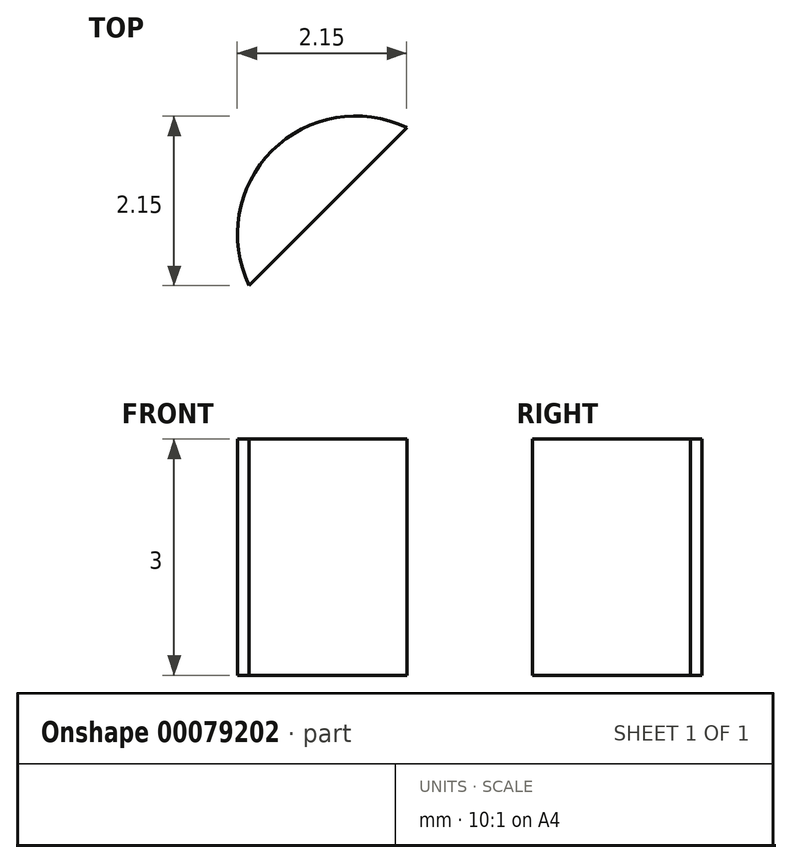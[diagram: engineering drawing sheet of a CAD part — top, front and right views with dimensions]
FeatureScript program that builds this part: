
annotation { "Feature Type Name" : "Feature", "Feature Type Description" : "" }
export const myFeature = defineFeature(function(context is Context, id is Id, definition is map)
    precondition{}
    {
        {
            var Q0;
            Q0=qCreatedBy(makeId("Top.planeOp"),FACE);
            var sketch = newSketch(context, id + "F0", { "sketchPlane" : qUnion([Q0])});
            skFitSpline(sketch, "E0.0.0", {"points": [v(-191, 0) * mm, v(-191, -31) * mm, v(-159.74, -92.2) * mm, v(-184.76, -197.17) * mm, v(-196.84, -201.33) * mm, v(-195.38, -204.68) * mm, v(-191.45, -211.03) * mm, v(-181.99, -213.22) * mm, v(-179.14, -216) * mm, v(-179.15, -231.75) * mm, v(-173.66, -257.8) * mm, v(-156.24, -267.72) * mm, v(-139.3, -271.16) * mm, v(-124.5, -267.12) * mm, v(-95.07, -253.88) * mm, v(-89.85, -257.77) * mm, v(-87.34, -261.97) * mm, v(-79.14, -275.56) * mm, v(0, -317.47) * mm, v(79.14, -275.56) * mm, v(87.34, -261.97) * mm, v(89.85, -257.77) * mm, v(95.07, -253.88) * mm, v(124.5, -267.11) * mm, v(139.3, -271.16) * mm, v(156.3, -267.7) * mm, v(173.4, -257.87) * mm, v(180.16, -231.44) * mm, v(176.53, -214.3) * mm, v(191.5, -211.34) * mm, v(195.34, -204.69) * mm, v(196.86, -201.33) * mm, v(184.74, -197.18) * mm, v(159.75, -92.2) * mm, v(206.83, 0) * mm, v(159.75, 92.2) * mm, v(184.74, 197.18) * mm, v(196.86, 201.33) * mm, v(195.34, 204.69) * mm, v(191.5, 211.34) * mm, v(176.53, 214.3) * mm, v(180.16, 231.44) * mm, v(173.4, 257.87) * mm, v(156.3, 267.7) * mm, v(139.3, 271.16) * mm, v(124.5, 267.11) * mm, v(95.07, 253.88) * mm, v(89.85, 257.77) * mm, v(87.34, 261.97) * mm, v(79.14, 275.56) * mm, v(0, 317.47) * mm, v(-79.14, 275.56) * mm, v(-87.34, 261.97) * mm, v(-89.85, 257.77) * mm, v(-95.07, 253.88) * mm, v(-124.5, 267.12) * mm, v(-139.3, 271.16) * mm, v(-156.24, 267.72) * mm, v(-173.66, 257.8) * mm, v(-179.15, 231.75) * mm, v(-179.14, 216) * mm, v(-181.99, 213.22) * mm, v(-191.45, 211.03) * mm, v(-195.38, 204.68) * mm, v(-196.84, 201.33) * mm, v(-184.76, 197.17) * mm, v(-159.74, 92.2) * mm, v(-191, 31) * mm, v(-191, 0) * mm]});
            skCircle(sketch, "E1.0", {"center": v(0, 192.5) * mm, "radius": 6 * mm});
            skCircle(sketch, "E2.0", {"center": v(0, -192.5) * mm, "radius": 6 * mm});
            skPoint(sketch, "E3.0", {"position": v(0, 0) * mm});
            skLineSegment(sketch, "E4", {"start": v(-243.03, 0) * mm, "end": v(337.73, 0) * mm, "construction": true});
            skLineSegment(sketch, "E5", {"start": v(0, 337.07) * mm, "end": v(0, -343.4) * mm, "construction": true});
            skFitSpline(sketch, "E6.0.0", {"points": [v(-146.48, 0) * mm, v(-146.48, -31.99) * mm, v(-89.5, -87.65) * mm, v(-140.83, -150.23) * mm, v(0, -234.29) * mm, v(140.83, -150.23) * mm, v(89.5, -87.65) * mm, v(179.22, 0) * mm, v(89.5, 87.65) * mm, v(140.83, 150.23) * mm, v(0, 234.29) * mm, v(-140.83, 150.23) * mm, v(-89.5, 87.65) * mm, v(-146.48, 31.99) * mm, v(-146.48, 0) * mm]});
            skEllipticalArc(sketch, "E6.0.1", {});
            skFitSpline(sketch, "E6.0.2", {"points": [v(-146.48, 0) * mm, v(-146.48, -31.99) * mm, v(-89.5, -87.65) * mm, v(-140.83, -150.23) * mm, v(0, -234.29) * mm, v(140.83, -150.23) * mm, v(89.5, -87.65) * mm, v(179.22, 0) * mm, v(89.5, 87.65) * mm, v(140.83, 150.23) * mm, v(0, 234.29) * mm, v(-140.83, 150.23) * mm, v(-89.5, 87.65) * mm, v(-146.48, 31.99) * mm, v(-146.48, 0) * mm]});
            skEllipticalArc(sketch, "E6.0.3", {});
            skCircle(sketch, "E7.0", {"center": v(102.5, -75) * mm, "radius": 5 * mm});
            skCircle(sketch, "E8.0", {"center": v(102.5, 75) * mm, "radius": 5 * mm});
            skCircle(sketch, "E9.0", {"center": v(-102.5, 75) * mm, "radius": 5 * mm});
            skCircle(sketch, "E10.0", {"center": v(-102.5, -75) * mm, "radius": 5 * mm});
            skLineSegment(sketch, "E11", {"start": v(0, 300) * mm, "end": v(0, 202.46) * mm, "construction": true});
            skPoint(sketch, "E12", {"position": v(-191, 0) * mm});
            skPoint(sketch, "E13", {"position": v(0, -287.33) * mm});
            skPoint(sketch, "E14.MirrorP", {"position": v(-178.8, 0) * mm});
            skPoint(sketch, "E15.MirrorP", {"position": v(-161, -94.7) * mm});
            skPoint(sketch, "E16.MirrorP", {"position": v(-135.27, -192.3) * mm});
            skPoint(sketch, "E17", {"position": v(-173.78, -187.11) * mm});
            skPoint(sketch, "E18", {"position": v(-169.04, -211.96) * mm});
            skPoint(sketch, "E19", {"position": v(-172.92, -206.07) * mm});
            skPoint(sketch, "E20", {"position": v(-163.34, -243.8) * mm});
            skPoint(sketch, "E21", {"position": v(-112.98, -248.73) * mm});
            skPoint(sketch, "E22", {"position": v(-72.32, -260) * mm});
            skPoint(sketch, "E23", {"position": v(-82.35, -247.43) * mm});
            skPoint(sketch, "E24", {"position": v(-91.92, -242.99) * mm});
            skPoint(sketch, "E25", {"position": v(-144.07, -257.6) * mm});
            skPoint(sketch, "E26", {"position": v(-180.24, -201.62) * mm});
            skLineSegment(sketch, "E27", {"start": v(0, 0) * mm, "end": v(0, 248.44) * mm, "construction": true});
            skLineSegment(sketch, "E28", {"start": v(154, 0) * mm, "end": v(-100.29, 0) * mm, "construction": true});
            skPoint(sketch, "E29.MirrorP", {"position": v(0, 287.33) * mm});
            skPoint(sketch, "E30.MirrorP", {"position": v(-82.35, 247.43) * mm});
            skPoint(sketch, "E31.MirrorP", {"position": v(-172.92, 206.07) * mm});
            skPoint(sketch, "E32.MirrorP", {"position": v(-112.98, 248.73) * mm});
            skPoint(sketch, "E33.MirrorP", {"position": v(-163.34, 243.8) * mm});
            skPoint(sketch, "E34.MirrorP", {"position": v(-161, 94.7) * mm});
            skPoint(sketch, "E35.MirrorP", {"position": v(-169.04, 211.96) * mm});
            skPoint(sketch, "E36.MirrorP", {"position": v(-173.78, 187.11) * mm});
            skPoint(sketch, "E37.MirrorP", {"position": v(-144.07, 257.6) * mm});
            skPoint(sketch, "E38.MirrorP", {"position": v(-180.24, 201.62) * mm});
            skPoint(sketch, "E39.MirrorP", {"position": v(-72.32, 260) * mm});
            skPoint(sketch, "E40.MirrorP", {"position": v(-91.92, 242.99) * mm});
            skLineSegment(sketch, "E41.MirrorCS", {"start": v(0, 0) * mm, "end": v(0, -248.44) * mm, "construction": true});
            skPoint(sketch, "E42.MirrorP", {"position": v(180.24, -201.62) * mm});
            skPoint(sketch, "E43.MirrorP", {"position": v(178.8, 0) * mm});
            skPoint(sketch, "E44.MirrorP", {"position": v(180.25, 201.62) * mm});
            skPoint(sketch, "E45.MirrorP", {"position": v(0.01, 287.33) * mm});
            skPoint(sketch, "E46.MirrorP", {"position": v(91.91, -242.99) * mm});
            skPoint(sketch, "E47.MirrorP", {"position": v(72.33, 260) * mm});
            skPoint(sketch, "E48.MirrorP", {"position": v(163.34, 243.8) * mm});
            skPoint(sketch, "E49.MirrorP", {"position": v(82.34, -247.43) * mm});
            skPoint(sketch, "E50.MirrorP", {"position": v(173.77, -187.12) * mm});
            skPoint(sketch, "E51.MirrorP", {"position": v(161, -94.7) * mm});
            skPoint(sketch, "E52.MirrorP", {"position": v(72.32, -260) * mm});
            skPoint(sketch, "E53.MirrorP", {"position": v(82.35, 247.43) * mm});
            skPoint(sketch, "E54.MirrorP", {"position": v(173.78, 187.1) * mm});
            skPoint(sketch, "E55.MirrorP", {"position": v(169.03, -211.97) * mm});
            skPoint(sketch, "E56.MirrorP", {"position": v(169.04, 211.96) * mm});
            skPoint(sketch, "E57.MirrorP", {"position": v(163.33, -243.8) * mm});
            skPoint(sketch, "E58.MirrorP", {"position": v(161, 94.7) * mm});
            skPoint(sketch, "E59.MirrorP", {"position": v(172.92, 206.07) * mm});
            skPoint(sketch, "E60.MirrorP", {"position": v(144.07, 257.6) * mm});
            skPoint(sketch, "E61.MirrorP", {"position": v(112.97, -248.73) * mm});
            skPoint(sketch, "E62.MirrorP", {"position": v(112.98, 248.72) * mm});
            skPoint(sketch, "E63.MirrorP", {"position": v(91.92, 242.98) * mm});
            skPoint(sketch, "E64.MirrorP", {"position": v(144.06, -257.61) * mm});
            skPoint(sketch, "E65.MirrorP", {"position": v(172.91, -206.08) * mm});
            skFitSpline(sketch, "E66", {"points": [v(0, -287.33) * mm, v(-72.32, -260) * mm, v(-82.35, -247.43) * mm, v(-91.92, -242.99) * mm, v(-112.98, -248.73) * mm, v(-144.07, -257.6) * mm, v(-163.34, -243.8) * mm, v(-169.04, -211.96) * mm, v(-172.92, -206.07) * mm, v(-180.24, -201.62) * mm, v(-173.78, -187.11) * mm, v(-161, -94.7) * mm, v(-178.8, 0) * mm, v(-161, 94.7) * mm, v(-173.78, 187.11) * mm, v(-180.24, 201.62) * mm, v(-172.92, 206.07) * mm, v(-169.04, 211.96) * mm, v(-163.34, 243.8) * mm, v(-144.07, 257.6) * mm, v(-112.98, 248.73) * mm, v(-91.92, 242.99) * mm, v(-82.35, 247.43) * mm, v(-72.32, 260) * mm, v(0, 287.33) * mm, v(72.33, 260) * mm, v(82.35, 247.43) * mm, v(91.92, 242.98) * mm, v(112.98, 248.72) * mm, v(144.07, 257.6) * mm, v(163.34, 243.8) * mm, v(169.04, 211.96) * mm, v(172.92, 206.07) * mm, v(180.25, 201.62) * mm, v(173.78, 187.1) * mm, v(161, 94.7) * mm, v(178.8, 0) * mm, v(161, -94.7) * mm, v(173.77, -187.12) * mm, v(180.24, -201.62) * mm, v(172.91, -206.08) * mm, v(169.03, -211.97) * mm, v(163.33, -243.8) * mm, v(144.06, -257.61) * mm, v(112.97, -248.73) * mm, v(91.91, -242.99) * mm, v(82.34, -247.43) * mm, v(72.32, -260) * mm, v(0, -287.33) * mm]});
            skFitSpline(sketch, "E67.0", {"points": [v(142.65, 79.63) * mm, v(142.7, 82.88) * mm, v(142.65, 86.13) * mm, v(142.47, 90.44) * mm, v(142.03, 95.8) * mm, v(141.15, 102.18) * mm, v(139.52, 110.6) * mm, v(136.63, 120.92) * mm, v(131.87, 132.9) * mm, v(125.85, 144.38) * mm, v(119.83, 153.47) * mm, v(114.42, 160.4) * mm, v(110.08, 165.43) * mm, v(106.22, 169.46) * mm, v(103, 172.58) * mm, v(100.52, 174.88) * mm, v(97.98, 177.11) * mm, v(94.52, 180.01) * mm, v(90.06, 183.47) * mm, v(84.52, 187.36) * mm, v(76.88, 192.2) * mm, v(66.91, 197.57) * mm, v(54.35, 202.92) * mm, v(41.3, 207.13) * mm, v(30.08, 209.68) * mm, v(20.94, 211.11) * mm, v(14.01, 211.9) * mm, v(8.2, 212.28) * mm, v(3.52, 212.44) * mm, v(0, 212.48) * mm, v(-3.52, 212.44) * mm, v(-8.2, 212.28) * mm, v(-14.01, 211.9) * mm, v(-20.94, 211.11) * mm, v(-30.08, 209.68) * mm, v(-41.3, 207.13) * mm, v(-54.35, 202.92) * mm, v(-66.91, 197.57) * mm, v(-76.88, 192.2) * mm, v(-84.52, 187.36) * mm, v(-90.06, 183.47) * mm, v(-94.52, 180.01) * mm, v(-97.98, 177.11) * mm, v(-100.52, 174.88) * mm, v(-103, 172.58) * mm, v(-106.22, 169.46) * mm, v(-110.08, 165.43) * mm, v(-114.42, 160.4) * mm, v(-119.83, 153.47) * mm, v(-125.85, 144.38) * mm, v(-131.87, 132.9) * mm, v(-136.63, 120.92) * mm, v(-139.52, 110.6) * mm, v(-141.15, 102.18) * mm, v(-142.03, 95.8) * mm, v(-142.47, 90.44) * mm, v(-142.65, 86.13) * mm, v(-142.7, 82.88) * mm, v(-142.65, 79.63) * mm, v(-142.47, 75.32) * mm, v(-142.03, 69.96) * mm, v(-141.15, 63.58) * mm, v(-139.52, 55.16) * mm, v(-136.63, 44.84) * mm, v(-131.87, 32.86) * mm, v(-125.85, 21.38) * mm, v(-119.83, 12.3) * mm, v(-114.42, 5.36) * mm, v(-110.08, 0.34) * mm, v(-106.22, -3.7) * mm, v(-103, -6.82) * mm, v(-100.52, -9.12) * mm, v(-97.98, -11.35) * mm, v(-94.52, -14.25) * mm, v(-90.06, -17.7) * mm, v(-84.52, -21.6) * mm, v(-76.88, -26.44) * mm, v(-66.91, -31.8) * mm, v(-54.35, -37.16) * mm, v(-41.3, -41.37) * mm, v(-30.08, -43.92) * mm, v(-20.94, -45.35) * mm, v(-14.01, -46.13) * mm, v(-8.2, -46.52) * mm, v(-3.52, -46.68) * mm, v(0, -46.72) * mm, v(3.52, -46.68) * mm, v(8.2, -46.52) * mm, v(14.01, -46.13) * mm, v(20.94, -45.35) * mm, v(30.08, -43.92) * mm, v(41.3, -41.37) * mm, v(54.35, -37.16) * mm, v(66.91, -31.8) * mm, v(76.88, -26.44) * mm, v(84.52, -21.6) * mm, v(90.06, -17.7) * mm, v(94.52, -14.25) * mm, v(97.98, -11.35) * mm, v(100.52, -9.12) * mm, v(103, -6.82) * mm, v(106.22, -3.7) * mm, v(110.08, 0.34) * mm, v(114.42, 5.36) * mm, v(119.83, 12.3) * mm, v(125.85, 21.38) * mm, v(131.87, 32.86) * mm, v(136.63, 44.84) * mm, v(139.52, 55.16) * mm, v(141.15, 63.58) * mm, v(142.03, 69.96) * mm, v(142.47, 75.32) * mm, v(142.65, 79.63) * mm, v(142.7, 82.88) * mm, v(142.65, 86.13) * mm]});
            skFitSpline(sketch, "E67.1", {"points": [v(-156.44, 2.63) * mm, v(-156.5, 0) * mm, v(-156.44, -2.63) * mm, v(-156.27, -5.23) * mm, v(-155.98, -7.8) * mm, v(-155.47, -11.2) * mm, v(-154.6, -15.39) * mm, v(-153.23, -20.3) * mm, v(-151.6, -25.1) * mm, v(-149.11, -31.37) * mm, v(-145.56, -38.98) * mm, v(-140.87, -47.75) * mm, v(-136.06, -56.17) * mm, v(-131.4, -64.24) * mm, v(-127.89, -70.62) * mm, v(-125.43, -75.48) * mm, v(-123.8, -78.98) * mm, v(-122.4, -82.33) * mm, v(-121.28, -85.5) * mm, v(-120.58, -87.96) * mm, v(-120.16, -89.82) * mm, v(-119.97, -90.93) * mm, v(-119.85, -91.8) * mm, v(-119.74, -92.65) * mm, v(-119.66, -93.72) * mm, v(-119.6, -95.02) * mm, v(-119.61, -96.75) * mm, v(-119.75, -98.96) * mm, v(-120.1, -101.68) * mm, v(-120.63, -104.5) * mm, v(-121.51, -108.4) * mm, v(-122.88, -113.52) * mm, v(-124.62, -120.16) * mm, v(-125.79, -126.17) * mm, v(-126.28, -131.32) * mm, v(-126.34, -135.36) * mm, v(-126.02, -139.54) * mm, v(-125.42, -142.76) * mm, v(-124.86, -144.92) * mm, v(-124.44, -146.37) * mm, v(-123.84, -148.16) * mm, v(-123, -150.27) * mm, v(-121.73, -153.05) * mm, v(-119.89, -156.44) * mm, v(-117.3, -160.4) * mm, v(-114.36, -164.24) * mm, v(-110, -169.23) * mm, v(-103.8, -175.22) * mm, v(-95.22, -182) * mm, v(-85.64, -188.33) * mm, v(-75.18, -194.13) * mm, v(-63.93, -199.32) * mm, v(-52.02, -203.8) * mm, v(-39.56, -207.5) * mm, v(-28.81, -209.82) * mm, v(-20.05, -211.16) * mm, v(-13.42, -211.9) * mm, v(-7.84, -212.28) * mm, v(-3.37, -212.44) * mm, v(0, -212.48) * mm, v(3.37, -212.44) * mm, v(7.84, -212.28) * mm, v(13.42, -211.9) * mm, v(20.05, -211.16) * mm, v(28.81, -209.82) * mm, v(39.56, -207.5) * mm, v(52.02, -203.8) * mm, v(63.93, -199.32) * mm, v(75.18, -194.13) * mm, v(85.64, -188.33) * mm, v(95.22, -182) * mm, v(103.8, -175.22) * mm, v(110, -169.23) * mm, v(114.36, -164.24) * mm, v(117.3, -160.4) * mm, v(119.89, -156.44) * mm, v(121.73, -153.05) * mm, v(123, -150.27) * mm, v(123.84, -148.16) * mm, v(124.44, -146.37) * mm, v(124.86, -144.92) * mm, v(125.42, -142.76) * mm, v(126.02, -139.54) * mm, v(126.34, -135.36) * mm, v(126.28, -131.32) * mm, v(125.79, -126.17) * mm, v(124.62, -120.16) * mm, v(122.88, -113.52) * mm, v(121.51, -108.4) * mm, v(120.63, -104.5) * mm, v(120.1, -101.68) * mm, v(119.75, -98.96) * mm, v(119.61, -96.75) * mm, v(119.6, -95.02) * mm, v(119.66, -93.72) * mm, v(119.74, -92.65) * mm, v(119.85, -91.8) * mm, v(119.97, -90.93) * mm, v(120.16, -89.82) * mm, v(120.58, -87.96) * mm, v(121.28, -85.5) * mm, v(122.4, -82.33) * mm, v(123.8, -78.98) * mm, v(125.43, -75.48) * mm, v(127.89, -70.62) * mm, v(131.4, -64.24) * mm, v(136.06, -56.17) * mm, v(140.87, -47.75) * mm, v(145.56, -38.98) * mm, v(149.11, -31.37) * mm, v(151.6, -25.1) * mm, v(153.23, -20.3) * mm, v(154.6, -15.39) * mm, v(155.47, -11.2) * mm, v(155.98, -7.8) * mm, v(156.27, -5.23) * mm, v(156.44, -2.63) * mm, v(156.5, 0) * mm, v(156.44, 2.63) * mm, v(156.27, 5.23) * mm, v(155.98, 7.8) * mm, v(155.47, 11.2) * mm, v(154.6, 15.39) * mm, v(153.23, 20.3) * mm, v(151.6, 25.1) * mm, v(149.11, 31.37) * mm, v(145.56, 38.97) * mm, v(140.87, 47.75) * mm, v(136.06, 56.17) * mm, v(131.4, 64.24) * mm, v(127.89, 70.62) * mm, v(125.43, 75.48) * mm, v(123.8, 78.98) * mm, v(122.4, 82.33) * mm, v(121.28, 85.5) * mm, v(120.58, 87.96) * mm, v(120.16, 89.82) * mm, v(119.97, 90.93) * mm, v(119.85, 91.8) * mm, v(119.74, 92.65) * mm, v(119.66, 93.72) * mm, v(119.6, 95.02) * mm, v(119.61, 96.75) * mm, v(119.75, 98.96) * mm, v(120.1, 101.68) * mm, v(120.63, 104.5) * mm, v(121.51, 108.4) * mm, v(122.88, 113.52) * mm, v(124.62, 120.16) * mm, v(125.79, 126.17) * mm, v(126.28, 131.32) * mm, v(126.34, 135.36) * mm, v(126.02, 139.54) * mm, v(125.42, 142.76) * mm, v(124.86, 144.92) * mm, v(124.44, 146.37) * mm, v(123.84, 148.16) * mm, v(123, 150.27) * mm, v(121.73, 153.05) * mm, v(119.89, 156.44) * mm, v(117.3, 160.4) * mm, v(114.36, 164.24) * mm, v(110, 169.23) * mm, v(103.8, 175.22) * mm, v(95.22, 182) * mm, v(85.64, 188.33) * mm, v(75.18, 194.13) * mm, v(63.93, 199.32) * mm, v(52.02, 203.8) * mm, v(39.56, 207.5) * mm, v(28.81, 209.82) * mm, v(20.05, 211.16) * mm, v(13.42, 211.9) * mm, v(7.84, 212.28) * mm, v(3.37, 212.44) * mm, v(0, 212.48) * mm, v(-3.37, 212.44) * mm, v(-7.84, 212.28) * mm, v(-13.42, 211.9) * mm, v(-20.05, 211.16) * mm, v(-28.81, 209.82) * mm, v(-39.56, 207.5) * mm, v(-52.02, 203.8) * mm, v(-63.93, 199.32) * mm, v(-75.18, 194.13) * mm, v(-85.64, 188.33) * mm, v(-95.22, 182) * mm, v(-103.8, 175.22) * mm, v(-110, 169.23) * mm, v(-114.36, 164.24) * mm, v(-117.3, 160.4) * mm, v(-119.89, 156.44) * mm, v(-121.73, 153.05) * mm, v(-123, 150.27) * mm, v(-123.84, 148.16) * mm, v(-124.44, 146.37) * mm, v(-124.86, 144.92) * mm, v(-125.42, 142.76) * mm, v(-126.02, 139.54) * mm, v(-126.34, 135.36) * mm, v(-126.28, 131.32) * mm, v(-125.79, 126.17) * mm, v(-124.62, 120.16) * mm, v(-122.88, 113.52) * mm, v(-121.51, 108.4) * mm, v(-120.63, 104.5) * mm, v(-120.1, 101.68) * mm, v(-119.75, 98.96) * mm, v(-119.61, 96.75) * mm, v(-119.6, 95.02) * mm, v(-119.66, 93.72) * mm, v(-119.74, 92.65) * mm, v(-119.85, 91.8) * mm, v(-119.97, 90.93) * mm, v(-120.16, 89.82) * mm, v(-120.58, 87.96) * mm, v(-121.28, 85.5) * mm, v(-122.4, 82.33) * mm, v(-123.8, 78.98) * mm, v(-125.43, 75.48) * mm, v(-127.89, 70.62) * mm, v(-131.4, 64.24) * mm, v(-136.06, 56.17) * mm, v(-140.87, 47.75) * mm, v(-145.56, 38.97) * mm, v(-149.11, 31.37) * mm, v(-151.6, 25.1) * mm, v(-153.23, 20.3) * mm, v(-154.6, 15.39) * mm, v(-155.47, 11.2) * mm, v(-155.98, 7.8) * mm, v(-156.27, 5.23) * mm, v(-156.44, 2.63) * mm, v(-156.5, 0) * mm, v(-156.44, -2.63) * mm]});
            skFitSpline(sketch, "E67.2", {"points": [v(142.65, 79.63) * mm, v(142.7, 82.88) * mm, v(142.65, 86.13) * mm, v(142.47, 90.44) * mm, v(142.03, 95.8) * mm, v(141.15, 102.18) * mm, v(139.52, 110.6) * mm, v(136.63, 120.92) * mm, v(131.87, 132.9) * mm, v(125.85, 144.38) * mm, v(119.83, 153.47) * mm, v(114.42, 160.4) * mm, v(110.08, 165.43) * mm, v(106.22, 169.46) * mm, v(103, 172.58) * mm, v(100.52, 174.88) * mm, v(97.98, 177.11) * mm, v(94.52, 180.01) * mm, v(90.06, 183.47) * mm, v(84.52, 187.36) * mm, v(76.88, 192.2) * mm, v(66.91, 197.57) * mm, v(54.35, 202.92) * mm, v(41.3, 207.13) * mm, v(30.08, 209.68) * mm, v(20.94, 211.11) * mm, v(14.01, 211.9) * mm, v(8.2, 212.28) * mm, v(3.52, 212.44) * mm, v(0, 212.48) * mm, v(-3.52, 212.44) * mm, v(-8.2, 212.28) * mm, v(-14.01, 211.9) * mm, v(-20.94, 211.11) * mm, v(-30.08, 209.68) * mm, v(-41.3, 207.13) * mm, v(-54.35, 202.92) * mm, v(-66.91, 197.57) * mm, v(-76.88, 192.2) * mm, v(-84.52, 187.36) * mm, v(-90.06, 183.47) * mm, v(-94.52, 180.01) * mm, v(-97.98, 177.11) * mm, v(-100.52, 174.88) * mm, v(-103, 172.58) * mm, v(-106.22, 169.46) * mm, v(-110.08, 165.43) * mm, v(-114.42, 160.4) * mm, v(-119.83, 153.47) * mm, v(-125.85, 144.38) * mm, v(-131.87, 132.9) * mm, v(-136.63, 120.92) * mm, v(-139.52, 110.6) * mm, v(-141.15, 102.18) * mm, v(-142.03, 95.8) * mm, v(-142.47, 90.44) * mm, v(-142.65, 86.13) * mm, v(-142.7, 82.88) * mm, v(-142.65, 79.63) * mm, v(-142.47, 75.32) * mm, v(-142.03, 69.96) * mm, v(-141.15, 63.58) * mm, v(-139.52, 55.16) * mm, v(-136.63, 44.84) * mm, v(-131.87, 32.86) * mm, v(-125.85, 21.38) * mm, v(-119.83, 12.3) * mm, v(-114.42, 5.36) * mm, v(-110.08, 0.34) * mm, v(-106.22, -3.7) * mm, v(-103, -6.82) * mm, v(-100.52, -9.12) * mm, v(-97.98, -11.35) * mm, v(-94.52, -14.25) * mm, v(-90.06, -17.7) * mm, v(-84.52, -21.6) * mm, v(-76.88, -26.44) * mm, v(-66.91, -31.8) * mm, v(-54.35, -37.16) * mm, v(-41.3, -41.37) * mm, v(-30.08, -43.92) * mm, v(-20.94, -45.35) * mm, v(-14.01, -46.13) * mm, v(-8.2, -46.52) * mm, v(-3.52, -46.68) * mm, v(0, -46.72) * mm, v(3.52, -46.68) * mm, v(8.2, -46.52) * mm, v(14.01, -46.13) * mm, v(20.94, -45.35) * mm, v(30.08, -43.92) * mm, v(41.3, -41.37) * mm, v(54.35, -37.16) * mm, v(66.91, -31.8) * mm, v(76.88, -26.44) * mm, v(84.52, -21.6) * mm, v(90.06, -17.7) * mm, v(94.52, -14.25) * mm, v(97.98, -11.35) * mm, v(100.52, -9.12) * mm, v(103, -6.82) * mm, v(106.22, -3.7) * mm, v(110.08, 0.34) * mm, v(114.42, 5.36) * mm, v(119.83, 12.3) * mm, v(125.85, 21.38) * mm, v(131.87, 32.86) * mm, v(136.63, 44.84) * mm, v(139.52, 55.16) * mm, v(141.15, 63.58) * mm, v(142.03, 69.96) * mm, v(142.47, 75.32) * mm, v(142.65, 79.63) * mm, v(142.7, 82.88) * mm, v(142.65, 86.13) * mm]});
            skFitSpline(sketch, "E67.3", {"points": [v(-156.44, 2.63) * mm, v(-156.5, 0) * mm, v(-156.44, -2.63) * mm, v(-156.27, -5.23) * mm, v(-155.98, -7.8) * mm, v(-155.47, -11.2) * mm, v(-154.6, -15.39) * mm, v(-153.23, -20.3) * mm, v(-151.6, -25.1) * mm, v(-149.11, -31.37) * mm, v(-145.56, -38.98) * mm, v(-140.87, -47.75) * mm, v(-136.06, -56.17) * mm, v(-131.4, -64.24) * mm, v(-127.89, -70.62) * mm, v(-125.43, -75.48) * mm, v(-123.8, -78.98) * mm, v(-122.4, -82.33) * mm, v(-121.28, -85.5) * mm, v(-120.58, -87.96) * mm, v(-120.16, -89.82) * mm, v(-119.97, -90.93) * mm, v(-119.85, -91.8) * mm, v(-119.74, -92.65) * mm, v(-119.66, -93.72) * mm, v(-119.6, -95.02) * mm, v(-119.61, -96.75) * mm, v(-119.75, -98.96) * mm, v(-120.1, -101.68) * mm, v(-120.63, -104.5) * mm, v(-121.51, -108.4) * mm, v(-122.88, -113.52) * mm, v(-124.62, -120.16) * mm, v(-125.79, -126.17) * mm, v(-126.28, -131.32) * mm, v(-126.34, -135.36) * mm, v(-126.02, -139.54) * mm, v(-125.42, -142.76) * mm, v(-124.86, -144.92) * mm, v(-124.44, -146.37) * mm, v(-123.84, -148.16) * mm, v(-123, -150.27) * mm, v(-121.73, -153.05) * mm, v(-119.89, -156.44) * mm, v(-117.3, -160.4) * mm, v(-114.36, -164.24) * mm, v(-110, -169.23) * mm, v(-103.8, -175.22) * mm, v(-95.22, -182) * mm, v(-85.64, -188.33) * mm, v(-75.18, -194.13) * mm, v(-63.93, -199.32) * mm, v(-52.02, -203.8) * mm, v(-39.56, -207.5) * mm, v(-28.81, -209.82) * mm, v(-20.05, -211.16) * mm, v(-13.42, -211.9) * mm, v(-7.84, -212.28) * mm, v(-3.37, -212.44) * mm, v(0, -212.48) * mm, v(3.37, -212.44) * mm, v(7.84, -212.28) * mm, v(13.42, -211.9) * mm, v(20.05, -211.16) * mm, v(28.81, -209.82) * mm, v(39.56, -207.5) * mm, v(52.02, -203.8) * mm, v(63.93, -199.32) * mm, v(75.18, -194.13) * mm, v(85.64, -188.33) * mm, v(95.22, -182) * mm, v(103.8, -175.22) * mm, v(110, -169.23) * mm, v(114.36, -164.24) * mm, v(117.3, -160.4) * mm, v(119.89, -156.44) * mm, v(121.73, -153.05) * mm, v(123, -150.27) * mm, v(123.84, -148.16) * mm, v(124.44, -146.37) * mm, v(124.86, -144.92) * mm, v(125.42, -142.76) * mm, v(126.02, -139.54) * mm, v(126.34, -135.36) * mm, v(126.28, -131.32) * mm, v(125.79, -126.17) * mm, v(124.62, -120.16) * mm, v(122.88, -113.52) * mm, v(121.51, -108.4) * mm, v(120.63, -104.5) * mm, v(120.1, -101.68) * mm, v(119.75, -98.96) * mm, v(119.61, -96.75) * mm, v(119.6, -95.02) * mm, v(119.66, -93.72) * mm, v(119.74, -92.65) * mm, v(119.85, -91.8) * mm, v(119.97, -90.93) * mm, v(120.16, -89.82) * mm, v(120.58, -87.96) * mm, v(121.28, -85.5) * mm, v(122.4, -82.33) * mm, v(123.8, -78.98) * mm, v(125.43, -75.48) * mm, v(127.89, -70.62) * mm, v(131.4, -64.24) * mm, v(136.06, -56.17) * mm, v(140.87, -47.75) * mm, v(145.56, -38.98) * mm, v(149.11, -31.37) * mm, v(151.6, -25.1) * mm, v(153.23, -20.3) * mm, v(154.6, -15.39) * mm, v(155.47, -11.2) * mm, v(155.98, -7.8) * mm, v(156.27, -5.23) * mm, v(156.44, -2.63) * mm, v(156.5, 0) * mm, v(156.44, 2.63) * mm, v(156.27, 5.23) * mm, v(155.98, 7.8) * mm, v(155.47, 11.2) * mm, v(154.6, 15.39) * mm, v(153.23, 20.3) * mm, v(151.6, 25.1) * mm, v(149.11, 31.37) * mm, v(145.56, 38.97) * mm, v(140.87, 47.75) * mm, v(136.06, 56.17) * mm, v(131.4, 64.24) * mm, v(127.89, 70.62) * mm, v(125.43, 75.48) * mm, v(123.8, 78.98) * mm, v(122.4, 82.33) * mm, v(121.28, 85.5) * mm, v(120.58, 87.96) * mm, v(120.16, 89.82) * mm, v(119.97, 90.93) * mm, v(119.85, 91.8) * mm, v(119.74, 92.65) * mm, v(119.66, 93.72) * mm, v(119.6, 95.02) * mm, v(119.61, 96.75) * mm, v(119.75, 98.96) * mm, v(120.1, 101.68) * mm, v(120.63, 104.5) * mm, v(121.51, 108.4) * mm, v(122.88, 113.52) * mm, v(124.62, 120.16) * mm, v(125.79, 126.17) * mm, v(126.28, 131.32) * mm, v(126.34, 135.36) * mm, v(126.02, 139.54) * mm, v(125.42, 142.76) * mm, v(124.86, 144.92) * mm, v(124.44, 146.37) * mm, v(123.84, 148.16) * mm, v(123, 150.27) * mm, v(121.73, 153.05) * mm, v(119.89, 156.44) * mm, v(117.3, 160.4) * mm, v(114.36, 164.24) * mm, v(110, 169.23) * mm, v(103.8, 175.22) * mm, v(95.22, 182) * mm, v(85.64, 188.33) * mm, v(75.18, 194.13) * mm, v(63.93, 199.32) * mm, v(52.02, 203.8) * mm, v(39.56, 207.5) * mm, v(28.81, 209.82) * mm, v(20.05, 211.16) * mm, v(13.42, 211.9) * mm, v(7.84, 212.28) * mm, v(3.37, 212.44) * mm, v(0, 212.48) * mm, v(-3.37, 212.44) * mm, v(-7.84, 212.28) * mm, v(-13.42, 211.9) * mm, v(-20.05, 211.16) * mm, v(-28.81, 209.82) * mm, v(-39.56, 207.5) * mm, v(-52.02, 203.8) * mm, v(-63.93, 199.32) * mm, v(-75.18, 194.13) * mm, v(-85.64, 188.33) * mm, v(-95.22, 182) * mm, v(-103.8, 175.22) * mm, v(-110, 169.23) * mm, v(-114.36, 164.24) * mm, v(-117.3, 160.4) * mm, v(-119.89, 156.44) * mm, v(-121.73, 153.05) * mm, v(-123, 150.27) * mm, v(-123.84, 148.16) * mm, v(-124.44, 146.37) * mm, v(-124.86, 144.92) * mm, v(-125.42, 142.76) * mm, v(-126.02, 139.54) * mm, v(-126.34, 135.36) * mm, v(-126.28, 131.32) * mm, v(-125.79, 126.17) * mm, v(-124.62, 120.16) * mm, v(-122.88, 113.52) * mm, v(-121.51, 108.4) * mm, v(-120.63, 104.5) * mm, v(-120.1, 101.68) * mm, v(-119.75, 98.96) * mm, v(-119.61, 96.75) * mm, v(-119.6, 95.02) * mm, v(-119.66, 93.72) * mm, v(-119.74, 92.65) * mm, v(-119.85, 91.8) * mm, v(-119.97, 90.93) * mm, v(-120.16, 89.82) * mm, v(-120.58, 87.96) * mm, v(-121.28, 85.5) * mm, v(-122.4, 82.33) * mm, v(-123.8, 78.98) * mm, v(-125.43, 75.48) * mm, v(-127.89, 70.62) * mm, v(-131.4, 64.24) * mm, v(-136.06, 56.17) * mm, v(-140.87, 47.75) * mm, v(-145.56, 38.97) * mm, v(-149.11, 31.37) * mm, v(-151.6, 25.1) * mm, v(-153.23, 20.3) * mm, v(-154.6, 15.39) * mm, v(-155.47, 11.2) * mm, v(-155.98, 7.8) * mm, v(-156.27, 5.23) * mm, v(-156.44, 2.63) * mm, v(-156.5, 0) * mm, v(-156.44, -2.63) * mm]});
            skLineSegment(sketch, "E68", {"start": v(134.34, -285.41) * mm, "end": v(106.05, -257.13) * mm});
            skLineSegment(sketch, "E69", {"start": v(91.91, -242.99) * mm, "end": v(106.05, -228.85) * mm});
            skLineSegment(sketch, "E70.0", {"start": v(77.77, -228.85) * mm, "end": v(91.91, -214.7) * mm});
            skLineSegment(sketch, "E71.0", {"start": v(106.05, -257.13) * mm, "end": v(120.2, -242.99) * mm});
            skLineSegment(sketch, "E72.0", {"start": v(119.86, -271.61) * mm, "end": v(134.34, -257.13) * mm});
            skLineSegment(sketch, "E73.0", {"start": v(63.63, -214.7) * mm, "end": v(77.77, -200.56) * mm});
            skLineSegment(sketch, "E74.0", {"start": v(49.48, -200.56) * mm, "end": v(63.63, -186.42) * mm});
            skLineSegment(sketch, "E75.0", {"start": v(35.34, -186.42) * mm, "end": v(120.2, -101.57) * mm});
            skLineSegment(sketch, "E76.0", {"start": v(21.2, -172.28) * mm, "end": v(120.2, -73.28) * mm});
            skLineSegment(sketch, "E77.0", {"start": v(7.06, -158.14) * mm, "end": v(106.05, -59.14) * mm});
            skLineSegment(sketch, "E78.0", {"start": v(-7.08, -144) * mm, "end": v(134.34, -2.57) * mm});
            skLineSegment(sketch, "E79.0", {"start": v(134.34, -285.41) * mm, "end": v(176.76, -242.99) * mm});
            skLineSegment(sketch, "E80.0", {"start": v(148.48, -271.27) * mm, "end": v(134.34, -257.13) * mm});
            skLineSegment(sketch, "E81.0", {"start": v(162.62, -257.13) * mm, "end": v(148.48, -242.99) * mm});
            skLineSegment(sketch, "E82.0", {"start": v(176.76, -242.99) * mm, "end": v(162.62, -228.85) * mm});
            skLineSegment(sketch, "E83.0", {"start": v(190.9, -228.85) * mm, "end": v(176.76, -214.7) * mm});
            skLineSegment(sketch, "E84.0", {"start": v(205.05, -214.7) * mm, "end": v(176.76, -186.42) * mm});
            skLineSegment(sketch, "E85.0", {"start": v(219.19, -200.56) * mm, "end": v(176.76, -158.14) * mm});
            skLineSegment(sketch, "E86.0", {"start": v(233.33, -186.42) * mm, "end": v(176.76, -129.85) * mm});
            skLineSegment(sketch, "E87.0", {"start": v(247.47, -172.28) * mm, "end": v(176.76, -101.57) * mm});
            skLineSegment(sketch, "E88.0", {"start": v(261.62, -158.14) * mm, "end": v(176.76, -73.28) * mm});
            skLineSegment(sketch, "E89.0", {"start": v(275.76, -144) * mm, "end": v(176.76, -45) * mm});
            skLineSegment(sketch, "E90.0", {"start": v(289.9, -129.85) * mm, "end": v(190.9, -30.86) * mm});
            skLineSegment(sketch, "E91", {"start": v(148.48, 11.57) * mm, "end": v(102.66, 57.4) * mm});
            skLineSegment(sketch, "E92", {"start": v(162.62, -2.57) * mm, "end": v(176.76, 11.57) * mm});
            skLineSegment(sketch, "E93", {"start": v(176.76, -16.71) * mm, "end": v(190.9, -2.57) * mm});
            skLineSegment(sketch, "E94", {"start": v(190.9, -30.86) * mm, "end": v(243.73, 21.97) * mm});
            skLineSegment(sketch, "E95", {"start": v(190.9, -30.86) * mm, "end": v(148.48, 11.57) * mm});
            skLineSegment(sketch, "E96", {"start": v(176.76, -45) * mm, "end": v(190.9, -30.86) * mm});
            skLineSegment(sketch, "E97", {"start": v(176.76, -45) * mm, "end": v(162.62, -30.86) * mm});
            skLineSegment(sketch, "E98", {"start": v(176.76, -73.28) * mm, "end": v(162.62, -59.14) * mm});
            skLineSegment(sketch, "E99", {"start": v(176.76, -73.28) * mm, "end": v(257.87, 7.83) * mm});
            skLineSegment(sketch, "E100", {"start": v(176.76, -101.57) * mm, "end": v(162.62, -87.42) * mm});
            skLineSegment(sketch, "E101", {"start": v(176.76, -101.57) * mm, "end": v(272.01, -6.32) * mm});
            skLineSegment(sketch, "E102", {"start": v(176.76, -129.85) * mm, "end": v(286.16, -20.46) * mm});
            skLineSegment(sketch, "E103", {"start": v(176.76, -129.85) * mm, "end": v(162.62, -115.7) * mm});
            skLineSegment(sketch, "E104", {"start": v(176.76, -158.14) * mm, "end": v(162.62, -144) * mm});
            skLineSegment(sketch, "E105", {"start": v(176.76, -158.14) * mm, "end": v(300.3, -34.6) * mm});
            skLineSegment(sketch, "E106", {"start": v(176.76, -186.42) * mm, "end": v(314.44, -48.74) * mm});
            skLineSegment(sketch, "E107", {"start": v(176.76, -186.42) * mm, "end": v(162.62, -172.28) * mm});
            skLineSegment(sketch, "E108", {"start": v(176.76, -214.7) * mm, "end": v(162.62, -200.56) * mm});
            skLineSegment(sketch, "E109", {"start": v(176.76, -214.7) * mm, "end": v(328.58, -62.88) * mm});
            skLineSegment(sketch, "E110", {"start": v(176.76, -242.99) * mm, "end": v(342.72, -77.03) * mm});
            skLineSegment(sketch, "E111", {"start": v(134.34, -257.13) * mm, "end": v(120.2, -242.99) * mm});
            skLineSegment(sketch, "E112", {"start": v(134.34, -257.13) * mm, "end": v(148.48, -242.99) * mm});
            skLineSegment(sketch, "E113", {"start": v(106.05, -257.13) * mm, "end": v(-52.9, -98.17) * mm});
            skPoint(sketch, "E114", {"position": v(91.91, -228.85) * mm});
            skPoint(sketch, "E115", {"position": v(77.77, -214.7) * mm});
            skPoint(sketch, "E116", {"position": v(63.63, -200.56) * mm});
            skLineSegment(sketch, "E117", {"start": v(63.63, -186.42) * mm, "end": v(-38.77, -84.03) * mm});
            skLineSegment(sketch, "E118", {"start": v(63.63, -186.42) * mm, "end": v(77.77, -172.28) * mm});
            skLineSegment(sketch, "E119", {"start": v(77.77, -172.28) * mm, "end": v(106.05, -144) * mm});
            skLineSegment(sketch, "E120", {"start": v(77.77, -172.28) * mm, "end": v(-24.62, -69.89) * mm});
            skLineSegment(sketch, "E121", {"start": v(91.91, -186.42) * mm, "end": v(91.91, -186.42) * mm});
            skLineSegment(sketch, "E122", {"start": v(91.91, -186.42) * mm, "end": v(106.05, -172.28) * mm});
            skLineSegment(sketch, "E123", {"start": v(77.77, -200.56) * mm, "end": v(91.91, -186.42) * mm});
            skLineSegment(sketch, "E124", {"start": v(77.77, -200.56) * mm, "end": v(63.63, -186.42) * mm});
            skLineSegment(sketch, "E125", {"start": v(91.91, -214.7) * mm, "end": v(77.77, -200.56) * mm});
            skLineSegment(sketch, "E126", {"start": v(91.91, -214.7) * mm, "end": v(106.05, -200.56) * mm});
            skLineSegment(sketch, "E127", {"start": v(106.05, -228.85) * mm, "end": v(91.91, -214.7) * mm});
            skLineSegment(sketch, "E128", {"start": v(106.05, -228.85) * mm, "end": v(120.2, -214.7) * mm});
            skLineSegment(sketch, "E129", {"start": v(120.2, -242.99) * mm, "end": v(106.05, -228.85) * mm});
            skLineSegment(sketch, "E130", {"start": v(120.2, -242.99) * mm, "end": v(134.34, -228.85) * mm});
            skLineSegment(sketch, "E131", {"start": v(148.48, -242.99) * mm, "end": v(134.34, -228.85) * mm});
            skLineSegment(sketch, "E132", {"start": v(148.48, -242.99) * mm, "end": v(162.62, -228.85) * mm});
            skLineSegment(sketch, "E133", {"start": v(134.34, -228.85) * mm, "end": v(120.2, -214.7) * mm});
            skLineSegment(sketch, "E134", {"start": v(134.34, -228.85) * mm, "end": v(148.48, -214.7) * mm});
            skLineSegment(sketch, "E135", {"start": v(120.2, -214.7) * mm, "end": v(106.05, -200.56) * mm});
            skLineSegment(sketch, "E136", {"start": v(120.2, -214.7) * mm, "end": v(134.34, -200.56) * mm});
            skLineSegment(sketch, "E137", {"start": v(106.05, -200.56) * mm, "end": v(77.77, -172.28) * mm});
            skLineSegment(sketch, "E138", {"start": v(106.05, -200.56) * mm, "end": v(120.2, -186.42) * mm});
            skPoint(sketch, "E139", {"position": v(106.05, -214.7) * mm});
            skPoint(sketch, "E140", {"position": v(77.77, -186.42) * mm});
            skLineSegment(sketch, "E141", {"start": v(106.05, -172.28) * mm, "end": v(-10.48, -55.74) * mm});
            skLineSegment(sketch, "E142", {"start": v(106.05, -172.28) * mm, "end": v(120.2, -158.14) * mm});
            skLineSegment(sketch, "E143", {"start": v(120.2, -186.42) * mm, "end": v(120.2, -186.42) * mm});
            skLineSegment(sketch, "E144", {"start": v(120.2, -186.42) * mm, "end": v(134.34, -172.28) * mm});
            skLineSegment(sketch, "E145", {"start": v(120.2, -186.42) * mm, "end": v(106.05, -172.28) * mm});
            skLineSegment(sketch, "E146", {"start": v(134.34, -200.56) * mm, "end": v(120.2, -186.42) * mm});
            skLineSegment(sketch, "E147", {"start": v(134.34, -200.56) * mm, "end": v(148.48, -186.42) * mm});
            skLineSegment(sketch, "E148", {"start": v(148.48, -214.7) * mm, "end": v(162.62, -200.56) * mm});
            skLineSegment(sketch, "E149", {"start": v(148.48, -214.7) * mm, "end": v(134.34, -200.56) * mm});
            skLineSegment(sketch, "E150", {"start": v(162.62, -228.85) * mm, "end": v(148.48, -214.7) * mm});
            skLineSegment(sketch, "E151", {"start": v(162.62, -228.85) * mm, "end": v(176.76, -214.7) * mm});
            skLineSegment(sketch, "E152", {"start": v(162.62, -200.56) * mm, "end": v(176.76, -186.42) * mm});
            skLineSegment(sketch, "E153", {"start": v(162.62, -200.56) * mm, "end": v(148.48, -186.42) * mm});
            skLineSegment(sketch, "E154", {"start": v(148.48, -186.42) * mm, "end": v(134.34, -172.28) * mm});
            skLineSegment(sketch, "E155", {"start": v(148.48, -186.42) * mm, "end": v(162.62, -172.28) * mm});
            skLineSegment(sketch, "E156", {"start": v(134.34, -172.28) * mm, "end": v(120.2, -158.14) * mm});
            skLineSegment(sketch, "E157", {"start": v(134.34, -172.28) * mm, "end": v(148.48, -158.14) * mm});
            skLineSegment(sketch, "E158", {"start": v(120.2, -158.14) * mm, "end": v(106.05, -144) * mm});
            skLineSegment(sketch, "E159", {"start": v(120.2, -158.14) * mm, "end": v(134.34, -144) * mm});
            skLineSegment(sketch, "E160", {"start": v(106.05, -144) * mm, "end": v(106.05, -144) * mm});
            skLineSegment(sketch, "E161", {"start": v(106.05, -144) * mm, "end": v(120.2, -129.85) * mm});
            skLineSegment(sketch, "E162", {"start": v(106.05, -144) * mm, "end": v(3.66, -41.6) * mm});
            skLineSegment(sketch, "E163", {"start": v(120.2, -129.85) * mm, "end": v(134.34, -115.7) * mm});
            skLineSegment(sketch, "E164", {"start": v(120.2, -129.85) * mm, "end": v(17.8, -27.46) * mm});
            skLineSegment(sketch, "E165", {"start": v(134.34, -144) * mm, "end": v(120.2, -129.85) * mm});
            skLineSegment(sketch, "E166", {"start": v(134.34, -144) * mm, "end": v(148.48, -129.85) * mm});
            skLineSegment(sketch, "E167", {"start": v(148.48, -158.14) * mm, "end": v(134.34, -144) * mm});
            skLineSegment(sketch, "E168", {"start": v(148.48, -158.14) * mm, "end": v(162.62, -144) * mm});
            skLineSegment(sketch, "E169", {"start": v(162.62, -172.28) * mm, "end": v(148.48, -158.14) * mm});
            skLineSegment(sketch, "E170", {"start": v(162.62, -172.28) * mm, "end": v(176.76, -158.14) * mm});
            skLineSegment(sketch, "E171", {"start": v(162.62, -144) * mm, "end": v(176.76, -129.85) * mm});
            skLineSegment(sketch, "E172", {"start": v(162.62, -144) * mm, "end": v(148.48, -129.85) * mm});
            skLineSegment(sketch, "E173", {"start": v(148.48, -129.85) * mm, "end": v(134.34, -115.7) * mm});
            skLineSegment(sketch, "E174", {"start": v(148.48, -129.85) * mm, "end": v(162.62, -115.7) * mm});
            skLineSegment(sketch, "E175", {"start": v(134.34, -115.7) * mm, "end": v(120.2, -101.57) * mm});
            skLineSegment(sketch, "E176", {"start": v(134.34, -115.7) * mm, "end": v(148.48, -101.57) * mm});
            skLineSegment(sketch, "E177", {"start": v(120.2, -101.57) * mm, "end": v(134.34, -87.42) * mm});
            skLineSegment(sketch, "E178", {"start": v(120.2, -101.57) * mm, "end": v(31.95, -13.32) * mm});
            skLineSegment(sketch, "E179", {"start": v(148.48, -101.57) * mm, "end": v(134.34, -87.42) * mm});
            skLineSegment(sketch, "E180", {"start": v(148.48, -101.57) * mm, "end": v(162.62, -87.42) * mm});
            skLineSegment(sketch, "E181", {"start": v(162.62, -115.7) * mm, "end": v(148.48, -101.57) * mm});
            skLineSegment(sketch, "E182", {"start": v(162.62, -115.7) * mm, "end": v(176.76, -101.57) * mm});
            skLineSegment(sketch, "E183", {"start": v(162.62, -87.42) * mm, "end": v(176.76, -73.28) * mm});
            skLineSegment(sketch, "E184", {"start": v(162.62, -87.42) * mm, "end": v(148.48, -73.28) * mm});
            skLineSegment(sketch, "E185", {"start": v(134.34, -87.42) * mm, "end": v(120.2, -73.28) * mm});
            skLineSegment(sketch, "E186", {"start": v(134.34, -87.42) * mm, "end": v(134.34, -87.42) * mm});
            skLineSegment(sketch, "E187", {"start": v(134.34, -87.42) * mm, "end": v(148.48, -73.28) * mm});
            skLineSegment(sketch, "E188", {"start": v(120.2, -73.28) * mm, "end": v(106.05, -59.14) * mm});
            skLineSegment(sketch, "E189", {"start": v(120.2, -73.28) * mm, "end": v(148.48, -45) * mm});
            skLineSegment(sketch, "E190", {"start": v(148.48, -73.28) * mm, "end": v(120.2, -45) * mm});
            skLineSegment(sketch, "E191", {"start": v(148.48, -73.28) * mm, "end": v(162.62, -59.14) * mm});
            skLineSegment(sketch, "E192", {"start": v(162.62, -59.14) * mm, "end": v(176.76, -45) * mm});
            skLineSegment(sketch, "E193", {"start": v(162.62, -59.14) * mm, "end": v(134.34, -30.86) * mm});
            skLineSegment(sketch, "E194", {"start": v(148.48, -45) * mm, "end": v(162.62, -30.86) * mm});
            skLineSegment(sketch, "E195", {"start": v(162.62, -30.86) * mm, "end": v(176.76, -16.71) * mm});
            skLineSegment(sketch, "E196", {"start": v(162.62, -30.86) * mm, "end": v(134.34, -2.57) * mm});
            skLineSegment(sketch, "E197", {"start": v(134.34, -30.86) * mm, "end": v(148.48, -16.71) * mm});
            skLineSegment(sketch, "E198", {"start": v(134.34, -30.86) * mm, "end": v(120.2, -16.71) * mm});
            skLineSegment(sketch, "E199", {"start": v(120.2, -45) * mm, "end": v(134.34, -30.86) * mm});
            skLineSegment(sketch, "E200", {"start": v(120.2, -45) * mm, "end": v(60.23, 14.97) * mm});
            skLineSegment(sketch, "E201", {"start": v(106.05, -59.14) * mm, "end": v(46.09, 0.83) * mm});
            skLineSegment(sketch, "E202", {"start": v(106.05, -59.14) * mm, "end": v(120.2, -45) * mm});
            skLineSegment(sketch, "E203", {"start": v(148.48, -16.71) * mm, "end": v(162.62, -2.57) * mm});
            skLineSegment(sketch, "E204.0", {"start": v(205.05, -16.71) * mm, "end": v(190.9, -2.57) * mm});
            skLineSegment(sketch, "E205", {"start": v(176.76, 11.57) * mm, "end": v(215.45, 50.25) * mm});
            skLineSegment(sketch, "E206", {"start": v(176.76, 11.57) * mm, "end": v(162.62, 25.71) * mm});
            skLineSegment(sketch, "E207", {"start": v(190.9, -2.57) * mm, "end": v(176.76, 11.57) * mm});
            skLineSegment(sketch, "E208", {"start": v(190.9, -2.57) * mm, "end": v(229.59, 36.11) * mm});
            skLineSegment(sketch, "E209", {"start": v(120.2, -16.71) * mm, "end": v(74.37, 29.1) * mm});
            skLineSegment(sketch, "E210", {"start": v(134.34, -2.57) * mm, "end": v(88.51, 43.25) * mm});
            skLineSegment(sketch, "E211", {"start": v(134.34, -2.57) * mm, "end": v(148.48, 11.57) * mm});
            skLineSegment(sketch, "E212", {"start": v(148.48, 11.57) * mm, "end": v(201.3, 64.4) * mm});
            skPoint(sketch, "E213", {"position": v(120.2, -228.85) * mm});
            skPoint(sketch, "E214", {"position": v(134.34, -242.99) * mm});
            skPoint(sketch, "E215", {"position": v(148.48, -228.85) * mm});
            skPoint(sketch, "E216", {"position": v(134.34, -214.7) * mm});
            skPoint(sketch, "E217", {"position": v(120.2, -200.56) * mm});
            skPoint(sketch, "E218", {"position": v(106.05, -186.42) * mm});
            skPoint(sketch, "E219", {"position": v(120.2, -172.28) * mm});
            skPoint(sketch, "E220", {"position": v(134.34, -186.42) * mm});
            skPoint(sketch, "E221", {"position": v(148.48, -200.56) * mm});
            skPoint(sketch, "E222", {"position": v(162.62, -214.7) * mm});
            skPoint(sketch, "E223", {"position": v(162.62, -200.56) * mm});
            skPoint(sketch, "E224", {"position": v(176.76, -200.56) * mm});
            skPoint(sketch, "E225", {"position": v(162.62, -186.42) * mm});
            skPoint(sketch, "E226", {"position": v(148.48, -172.28) * mm});
            skPoint(sketch, "E227", {"position": v(148.48, -158.14) * mm});
            skPoint(sketch, "E228", {"position": v(162.62, -158.14) * mm});
            skPoint(sketch, "E229", {"position": v(176.76, -172.28) * mm});
            skPoint(sketch, "E230", {"position": v(134.34, -158.14) * mm});
            skPoint(sketch, "E231", {"position": v(148.48, -144) * mm});
            skPoint(sketch, "E232", {"position": v(120.2, -144) * mm});
            skPoint(sketch, "E233", {"position": v(134.34, -129.85) * mm});
            skPoint(sketch, "E234", {"position": v(162.62, -129.85) * mm});
            skPoint(sketch, "E235", {"position": v(148.48, -115.7) * mm});
            skPoint(sketch, "E236", {"position": v(120.2, -129.85) * mm});
            skPoint(sketch, "E237", {"position": v(120.2, -115.7) * mm});
            skPoint(sketch, "E238", {"position": v(134.34, -101.57) * mm});
            skPoint(sketch, "E239", {"position": v(162.62, -101.57) * mm});
            skPoint(sketch, "E240", {"position": v(148.48, -87.42) * mm});
            skPoint(sketch, "E241", {"position": v(134.34, -73.28) * mm});
            skPoint(sketch, "E242", {"position": v(148.48, -59.14) * mm});
            skPoint(sketch, "E243", {"position": v(162.62, -45) * mm});
            skPoint(sketch, "E244", {"position": v(148.48, -30.86) * mm});
            skPoint(sketch, "E245", {"position": v(176.76, -30.86) * mm});
            skPoint(sketch, "E246", {"position": v(162.62, -16.71) * mm});
            skPoint(sketch, "E247", {"position": v(176.76, -2.57) * mm});
            skPoint(sketch, "E248", {"position": v(162.62, -73.28) * mm});
            skCircle(sketch, "E249", {"center": v(120.2, -228.85) * mm, "radius": 2 * mm});
            skCircle(sketch, "E250", {"center": v(91.91, -214.7) * mm, "radius": 1 * mm});
            skCircle(sketch, "E251", {"center": v(94.03, -212.58) * mm, "radius": 1 * mm});
            skCircle(sketch, "E252", {"center": v(96.15, -210.46) * mm, "radius": 1 * mm});
            skCircle(sketch, "E253", {"center": v(94.03, -216.82) * mm, "radius": 1 * mm});
            skCircle(sketch, "E254", {"center": v(96.15, -218.95) * mm, "radius": 1 * mm});
            skCircle(sketch, "E255", {"center": v(89.79, -216.82) * mm, "radius": 1 * mm});
            skCircle(sketch, "E256", {"center": v(87.67, -218.95) * mm, "radius": 1 * mm});
            skCircle(sketch, "E257", {"center": v(89.79, -212.58) * mm, "radius": 1 * mm});
            skCircle(sketch, "E258", {"center": v(87.67, -210.46) * mm, "radius": 1 * mm});
            skCircle(sketch, "E259", {"center": v(106.05, -228.85) * mm, "radius": 1 * mm});
            skCircle(sketch, "E260", {"center": v(108.17, -226.72) * mm, "radius": 1 * mm});
            skCircle(sketch, "E261", {"center": v(110.3, -224.6) * mm, "radius": 1 * mm});
            skCircle(sketch, "E262", {"center": v(108.17, -230.97) * mm, "radius": 1 * mm});
            skCircle(sketch, "E263", {"center": v(110.3, -233.09) * mm, "radius": 1 * mm});
            skCircle(sketch, "E264", {"center": v(103.93, -230.97) * mm, "radius": 1 * mm});
            skCircle(sketch, "E265", {"center": v(101.81, -233.09) * mm, "radius": 1 * mm});
            skCircle(sketch, "E266", {"center": v(103.93, -226.72) * mm, "radius": 1 * mm});
            skCircle(sketch, "E267", {"center": v(101.81, -224.6) * mm, "radius": 1 * mm});
            skCircle(sketch, "E268", {"center": v(120.2, -242.99) * mm, "radius": 1 * mm});
            skCircle(sketch, "E269", {"center": v(122.32, -240.87) * mm, "radius": 1 * mm});
            skCircle(sketch, "E270", {"center": v(124.44, -238.75) * mm, "radius": 1 * mm});
            skCircle(sketch, "E271", {"center": v(122.32, -245.1) * mm, "radius": 1 * mm});
            skCircle(sketch, "E272", {"center": v(124.44, -247.23) * mm, "radius": 1 * mm});
            skCircle(sketch, "E273", {"center": v(118.07, -245.1) * mm, "radius": 1 * mm});
            skCircle(sketch, "E274", {"center": v(115.95, -247.23) * mm, "radius": 1 * mm});
            skCircle(sketch, "E275", {"center": v(118.07, -240.87) * mm, "radius": 1 * mm});
            skCircle(sketch, "E276", {"center": v(115.95, -238.75) * mm, "radius": 1 * mm});
            skCircle(sketch, "E277", {"center": v(77.77, -200.56) * mm, "radius": 1 * mm});
            skCircle(sketch, "E278", {"center": v(79.89, -198.44) * mm, "radius": 1 * mm});
            skCircle(sketch, "E279", {"center": v(82.01, -196.32) * mm, "radius": 1 * mm});
            skCircle(sketch, "E280", {"center": v(79.89, -202.68) * mm, "radius": 1 * mm});
            skCircle(sketch, "E281", {"center": v(82.01, -204.8) * mm, "radius": 1 * mm});
            skCircle(sketch, "E282", {"center": v(75.65, -202.68) * mm, "radius": 1 * mm});
            skCircle(sketch, "E283", {"center": v(73.53, -204.8) * mm, "radius": 1 * mm});
            skCircle(sketch, "E284", {"center": v(75.65, -198.44) * mm, "radius": 1 * mm});
            skCircle(sketch, "E285", {"center": v(73.53, -196.32) * mm, "radius": 1 * mm});
            skCircle(sketch, "E286", {"center": v(148.48, -242.99) * mm, "radius": 1 * mm});
            skCircle(sketch, "E287", {"center": v(150.6, -240.87) * mm, "radius": 1 * mm});
            skCircle(sketch, "E288", {"center": v(152.72, -238.75) * mm, "radius": 1 * mm});
            skCircle(sketch, "E289", {"center": v(150.6, -245.1) * mm, "radius": 1 * mm});
            skCircle(sketch, "E290", {"center": v(152.72, -247.23) * mm, "radius": 1 * mm});
            skCircle(sketch, "E291", {"center": v(146.36, -245.1) * mm, "radius": 1 * mm});
            skCircle(sketch, "E292", {"center": v(144.24, -247.23) * mm, "radius": 1 * mm});
            skCircle(sketch, "E293", {"center": v(146.36, -240.87) * mm, "radius": 1 * mm});
            skCircle(sketch, "E294", {"center": v(144.24, -238.75) * mm, "radius": 1 * mm});
            skCircle(sketch, "E295", {"center": v(134.34, -228.85) * mm, "radius": 1 * mm});
            skCircle(sketch, "E296", {"center": v(136.46, -226.72) * mm, "radius": 1 * mm});
            skCircle(sketch, "E297", {"center": v(138.58, -224.6) * mm, "radius": 1 * mm});
            skCircle(sketch, "E298", {"center": v(136.46, -230.97) * mm, "radius": 1 * mm});
            skCircle(sketch, "E299", {"center": v(138.58, -233.09) * mm, "radius": 1 * mm});
            skCircle(sketch, "E300", {"center": v(132.22, -230.97) * mm, "radius": 1 * mm});
            skCircle(sketch, "E301", {"center": v(130.1, -233.09) * mm, "radius": 1 * mm});
            skCircle(sketch, "E302", {"center": v(132.22, -226.72) * mm, "radius": 1 * mm});
            skCircle(sketch, "E303", {"center": v(130.1, -224.6) * mm, "radius": 1 * mm});
            skCircle(sketch, "E304", {"center": v(120.2, -214.7) * mm, "radius": 1 * mm});
            skCircle(sketch, "E305", {"center": v(122.32, -212.58) * mm, "radius": 1 * mm});
            skCircle(sketch, "E306", {"center": v(124.44, -210.46) * mm, "radius": 1 * mm});
            skCircle(sketch, "E307", {"center": v(122.32, -216.82) * mm, "radius": 1 * mm});
            skCircle(sketch, "E308", {"center": v(124.44, -218.95) * mm, "radius": 1 * mm});
            skCircle(sketch, "E309", {"center": v(118.07, -216.82) * mm, "radius": 1 * mm});
            skCircle(sketch, "E310", {"center": v(115.95, -218.95) * mm, "radius": 1 * mm});
            skCircle(sketch, "E311", {"center": v(118.07, -212.58) * mm, "radius": 1 * mm});
            skCircle(sketch, "E312", {"center": v(115.95, -210.46) * mm, "radius": 1 * mm});
            skCircle(sketch, "E313", {"center": v(106.05, -200.56) * mm, "radius": 1 * mm});
            skCircle(sketch, "E314", {"center": v(108.17, -198.44) * mm, "radius": 1 * mm});
            skCircle(sketch, "E315", {"center": v(110.3, -196.32) * mm, "radius": 1 * mm});
            skCircle(sketch, "E316", {"center": v(108.17, -202.68) * mm, "radius": 1 * mm});
            skCircle(sketch, "E317", {"center": v(110.3, -204.8) * mm, "radius": 1 * mm});
            skCircle(sketch, "E318", {"center": v(103.93, -202.68) * mm, "radius": 1 * mm});
            skCircle(sketch, "E319", {"center": v(101.81, -204.8) * mm, "radius": 1 * mm});
            skCircle(sketch, "E320", {"center": v(103.93, -198.44) * mm, "radius": 1 * mm});
            skCircle(sketch, "E321", {"center": v(101.81, -196.32) * mm, "radius": 1 * mm});
            skCircle(sketch, "E322", {"center": v(91.91, -186.42) * mm, "radius": 1 * mm});
            skCircle(sketch, "E323", {"center": v(94.03, -184.3) * mm, "radius": 1 * mm});
            skCircle(sketch, "E324", {"center": v(96.15, -182.18) * mm, "radius": 1 * mm});
            skCircle(sketch, "E325", {"center": v(94.03, -188.54) * mm, "radius": 1 * mm});
            skCircle(sketch, "E326", {"center": v(96.15, -190.66) * mm, "radius": 1 * mm});
            skCircle(sketch, "E327", {"center": v(89.79, -188.54) * mm, "radius": 1 * mm});
            skCircle(sketch, "E328", {"center": v(87.67, -190.66) * mm, "radius": 1 * mm});
            skCircle(sketch, "E329", {"center": v(89.79, -184.3) * mm, "radius": 1 * mm});
            skCircle(sketch, "E330", {"center": v(87.67, -182.18) * mm, "radius": 1 * mm});
            skCircle(sketch, "E331", {"center": v(162.62, -228.85) * mm, "radius": 1 * mm});
            skCircle(sketch, "E332", {"center": v(164.74, -226.72) * mm, "radius": 1 * mm});
            skCircle(sketch, "E333", {"center": v(166.86, -224.6) * mm, "radius": 1 * mm});
            skCircle(sketch, "E334", {"center": v(164.74, -230.97) * mm, "radius": 1 * mm});
            skCircle(sketch, "E335", {"center": v(166.86, -233.09) * mm, "radius": 1 * mm});
            skCircle(sketch, "E336", {"center": v(160.5, -230.97) * mm, "radius": 1 * mm});
            skCircle(sketch, "E337", {"center": v(158.38, -233.09) * mm, "radius": 1 * mm});
            skCircle(sketch, "E338", {"center": v(160.5, -226.72) * mm, "radius": 1 * mm});
            skCircle(sketch, "E339", {"center": v(158.38, -224.6) * mm, "radius": 1 * mm});
            skCircle(sketch, "E340", {"center": v(148.48, -214.7) * mm, "radius": 1 * mm});
            skCircle(sketch, "E341", {"center": v(150.6, -212.58) * mm, "radius": 1 * mm});
            skCircle(sketch, "E342", {"center": v(152.72, -210.46) * mm, "radius": 1 * mm});
            skCircle(sketch, "E343", {"center": v(150.6, -216.82) * mm, "radius": 1 * mm});
            skCircle(sketch, "E344", {"center": v(152.72, -218.95) * mm, "radius": 1 * mm});
            skCircle(sketch, "E345", {"center": v(146.36, -216.82) * mm, "radius": 1 * mm});
            skCircle(sketch, "E346", {"center": v(144.24, -218.95) * mm, "radius": 1 * mm});
            skCircle(sketch, "E347", {"center": v(146.36, -212.58) * mm, "radius": 1 * mm});
            skCircle(sketch, "E348", {"center": v(144.24, -210.46) * mm, "radius": 1 * mm});
            skCircle(sketch, "E349", {"center": v(134.34, -200.56) * mm, "radius": 1 * mm});
            skCircle(sketch, "E350", {"center": v(136.46, -198.44) * mm, "radius": 1 * mm});
            skCircle(sketch, "E351", {"center": v(138.58, -196.32) * mm, "radius": 1 * mm});
            skCircle(sketch, "E352", {"center": v(136.46, -202.68) * mm, "radius": 1 * mm});
            skCircle(sketch, "E353", {"center": v(138.58, -204.8) * mm, "radius": 1 * mm});
            skCircle(sketch, "E354", {"center": v(132.22, -202.68) * mm, "radius": 1 * mm});
            skCircle(sketch, "E355", {"center": v(130.1, -204.8) * mm, "radius": 1 * mm});
            skCircle(sketch, "E356", {"center": v(132.22, -198.44) * mm, "radius": 1 * mm});
            skCircle(sketch, "E357", {"center": v(130.1, -196.32) * mm, "radius": 1 * mm});
            skCircle(sketch, "E358", {"center": v(106.4, -172.63) * mm, "radius": 1.5 * mm});
            const initialGuessF0  = {"E6.0.1": [-4.768990313763766e-09, 0.08288086198017516, 1, 0, 0.13267715999999996, 0.11958350000000001, 1.901114383451003, 2.623263156960301], "E6.0.3": [-4.7689924231875125e-09, 0.08288086198017927, 1, 0, 0.13267715999999996, 0.11958350000000001, 0.5183294966667867, 1.2404782701360793]};
            skSetInitialGuess(sketch, initialGuessF0);
            skSolve(sketch);
        }
        {
            var Q0;
            {var subQ0=sQuery(id+"F0.wireOp",EDGE,"E145");var subQ1=sQuery(id+"F0.wireOp",EDGE,"E67.1");var subQ2=makeQuery(id+"F0.imprint","INTERSECT",VERTEX,{"derivedFrom":[subQ1,subQ0]});Q0=makeQuery(id+"F0.imprint","IMPRINT",FACE,{"disambiguationData":[TD([[makeQuery(id+"F0.imprint","IMPRINT",EDGE,{"disambiguationData":[TD([[subQ2,-1.0]])],"derivedFrom":subQ1}),-1.0]])]});}
            var Q1;
            {var subQ0=sQuery(id+"F0.wireOp",EDGE,"E145");var subQ1=sQuery(id+"F0.wireOp",EDGE,"E67.1");var subQ2=makeQuery(id+"F0.imprint","INTERSECT",VERTEX,{"derivedFrom":[subQ1,subQ0]});Q1=makeQuery(id+"F0.imprint","IMPRINT",FACE,{"disambiguationData":[TD([[makeQuery(id+"F0.imprint","IMPRINT",EDGE,{"disambiguationData":[TD([[subQ2,-1.0]])],"derivedFrom":subQ1}),1.0]])]});}
            var Q2;
            {var subQ1=sQuery(id+"F0.wireOp",EDGE,"E141");var subQ3=sQuery(id+"F0.wireOp",EDGE,"E358");var subQ4=makeQuery(id+"F0.imprint","INTERSECT",VERTEX,{"derivedFrom":[subQ1,subQ3]});Q2=makeQuery(id+"F0.imprint","IMPRINT",FACE,{"disambiguationData":[TD([[makeQuery(id+"F0.imprint","IMPRINT",EDGE,{"disambiguationData":[TD([[subQ4,1.0]])],"derivedFrom":subQ3}),1.0]])]});}
            var Q3;
            {var subQ1=sQuery(id+"F0.wireOp",EDGE,"E122");var subQ3=sQuery(id+"F0.wireOp",EDGE,"E358");var subQ4=makeQuery(id+"F0.imprint","INTERSECT",VERTEX,{"derivedFrom":[subQ1,subQ3]});Q3=makeQuery(id+"F0.imprint","IMPRINT",FACE,{"disambiguationData":[TD([[makeQuery(id+"F0.imprint","IMPRINT",EDGE,{"disambiguationData":[TD([[subQ4,1.0]])],"derivedFrom":subQ3}),1.0]])]});}
            var Q4;
            {var subQ0=sQuery(id+"F0.wireOp",EDGE,"E358");var subQ1=sQuery(id+"F0.wireOp",EDGE,"E67.1");var subQ2=makeQuery(id+"F0.imprint","INTERSECT",VERTEX,{"disambiguationData":[OD(0.0)],"derivedFrom":[subQ1,subQ0]});Q4=makeQuery(id+"F0.imprint","IMPRINT",FACE,{"disambiguationData":[TD([[makeQuery(id+"F0.imprint","IMPRINT",EDGE,{"disambiguationData":[TD([[subQ2,-1.0]])],"derivedFrom":subQ1}),1.0]])]});}
            var Q5;
            {var subQ0=sQuery(id+"F0.wireOp",EDGE,"E358");var subQ1=sQuery(id+"F0.wireOp",EDGE,"E67.1");var subQ2=makeQuery(id+"F0.imprint","INTERSECT",VERTEX,{"disambiguationData":[OD(0.0)],"derivedFrom":[subQ1,subQ0]});Q5=makeQuery(id+"F0.imprint","IMPRINT",FACE,{"disambiguationData":[TD([[makeQuery(id+"F0.imprint","IMPRINT",EDGE,{"disambiguationData":[TD([[subQ2,-1.0]])],"derivedFrom":subQ1}),-1.0]])]});}
            extrude(context, id + "F1", {"entities" : qUnion([Q0, Q1, Q2, Q3, Q4, Q5]), "depth" : 3 * mm, "offsetDistance" : 25 * mm});
        }
    });
